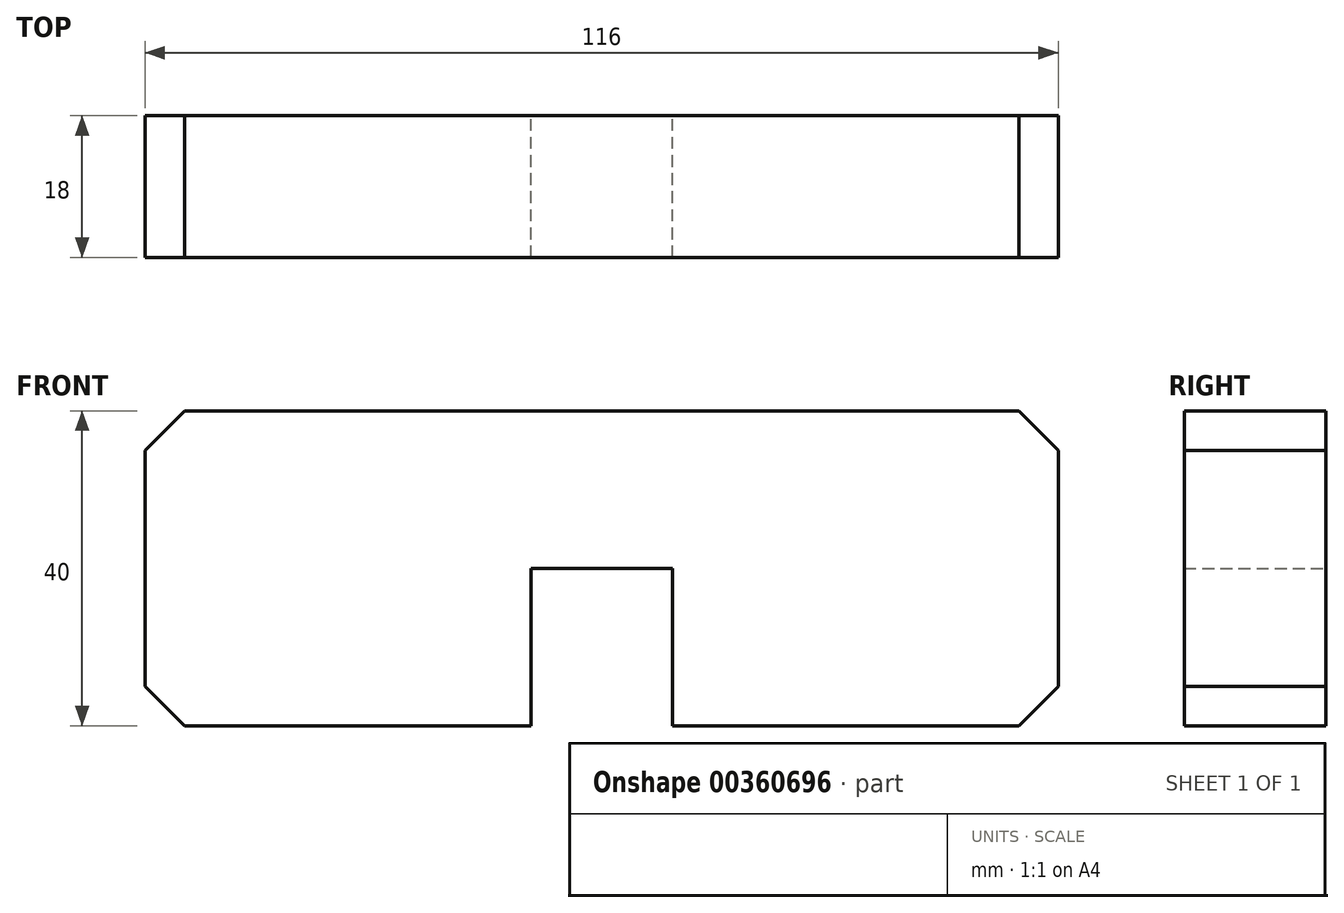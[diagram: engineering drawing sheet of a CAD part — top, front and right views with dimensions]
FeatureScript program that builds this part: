
annotation { "Feature Type Name" : "Feature", "Feature Type Description" : "" }
export const myFeature = defineFeature(function(context is Context, id is Id, definition is map)
    precondition{}
    {
        {
            var Q0;
            Q0=qCreatedBy(makeId("Front.planeOp"),FACE);
            var sketch = newSketch(context, id + "F0", { "sketchPlane" : qUnion([Q0])});
            skLineSegment(sketch, "E0.top", {"start": v(-9, 20) * mm, "end": v(9, 20) * mm});
            skLineSegment(sketch, "E0.left", {"start": v(-9, 0) * mm, "end": v(-9, 20) * mm});
            skLineSegment(sketch, "E0.right", {"start": v(9, 0) * mm, "end": v(9, 20) * mm});
            skLineSegment(sketch, "E1.bottom", {"start": v(-58, 0) * mm, "end": v(-9, 0) * mm});
            skLineSegment(sketch, "E1.top", {"start": v(-58, 40) * mm, "end": v(58, 40) * mm});
            skLineSegment(sketch, "E1.left", {"start": v(-58, 0) * mm, "end": v(-58, 40) * mm});
            skLineSegment(sketch, "E1.right", {"start": v(58, 0) * mm, "end": v(58, 40) * mm});
            skLineSegment(sketch, "E2.trimOffspring", {"start": v(9, 0) * mm, "end": v(58, 0) * mm});
            skSolve(sketch);
        }
        {
            var Q0;
            Q0=makeQuery(id+"F0.imprint","IMPRINT",FACE,{"disambiguationData":[TD([[makeQuery(id+"F0.imprint","IMPRINT",EDGE,{"derivedFrom":sQuery(id+"F0.wireOp",EDGE,"E0.top")}),1.0]])]});
            extrude(context, id + "F1", {"entities" : qUnion([Q0]), "depth" : 18 * mm});
        }
        {
            var Q0;
            Q0=makeQuery(id+"F1.opExtrude","SWEPT_EDGE",EDGE,{"disambiguationData":[OSD([sQuery(id+"F0.wireOp",EDGE,"E1.bottom"),sQuery(id+"F0.wireOp",EDGE,"E1.left")])]});
            var Q1;
            Q1=makeQuery(id+"F1.opExtrude","SWEPT_EDGE",EDGE,{"disambiguationData":[OSD([sQuery(id+"F0.wireOp",EDGE,"E1.right"),sQuery(id+"F0.wireOp",EDGE,"E2.trimOffspring")])]});
            var Q2;
            Q2=makeQuery(id+"F1.opExtrude","SWEPT_EDGE",EDGE,{"disambiguationData":[OSD([sQuery(id+"F0.wireOp",EDGE,"E1.top"),sQuery(id+"F0.wireOp",EDGE,"E1.right")])]});
            var Q3;
            Q3=makeQuery(id+"F1.opExtrude","SWEPT_EDGE",EDGE,{"disambiguationData":[OSD([sQuery(id+"F0.wireOp",EDGE,"E1.top"),sQuery(id+"F0.wireOp",EDGE,"E1.left")])]});
            chamfer(context, id + "F2", {"entities" : qUnion([Q0, Q1, Q2, Q3]), "width" : 5 * mm, "tangentPropagation" : true});
        }
    });
